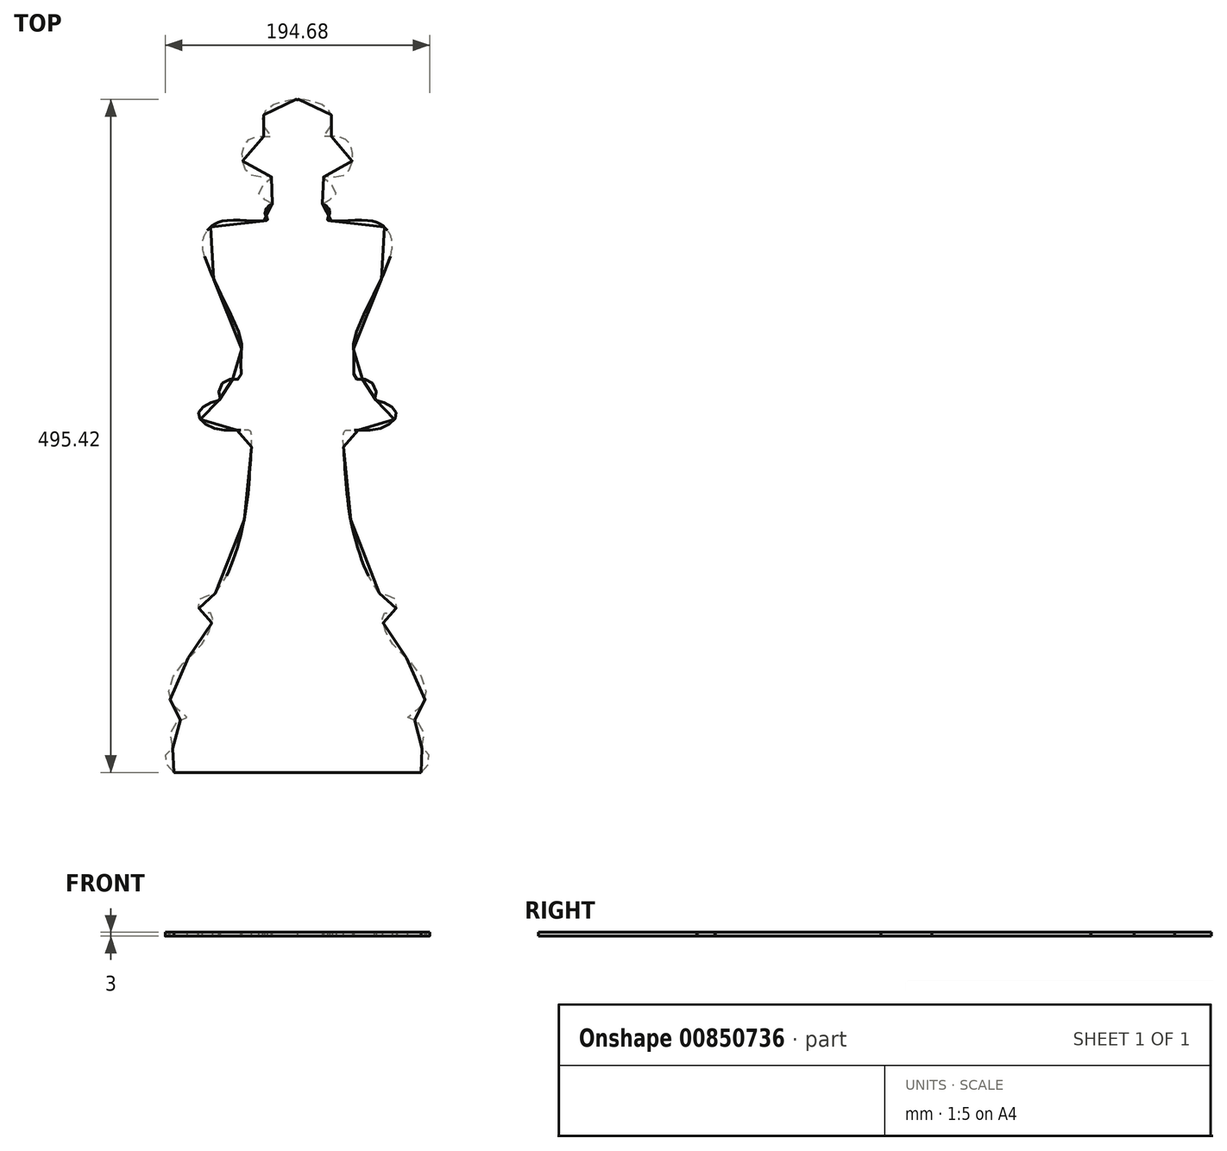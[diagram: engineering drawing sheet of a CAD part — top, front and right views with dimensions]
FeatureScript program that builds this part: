
annotation { "Feature Type Name" : "Feature", "Feature Type Description" : "" }
export const myFeature = defineFeature(function(context is Context, id is Id, definition is map)
    precondition{}
    {
        {
            var Q0;
            Q0=qCreatedBy(makeId("Top.planeOp"),FACE);
            var sketch = newSketch(context, id + "F0", { "sketchPlane" : qUnion([Q0])});
            skLineSegment(sketch, "E0", {"start": v(-250, 250) * mm, "end": v(250, -250) * mm, "construction": true});
            skLineSegment(sketch, "E1", {"start": v(250, 250) * mm, "end": v(-250, -250) * mm, "construction": true});
            skPoint(sketch, "E2", {"position": v(0, 0) * mm});
            skLineSegment(sketch, "E3", {"start": v(0, 250.01) * mm, "end": v(0, -249.99) * mm});
            skLineSegment(sketch, "E4", {"start": v(0, -249.99) * mm, "end": v(-90.99, -249.99) * mm});
            skFitSpline(sketch, "E5", {"points": [v(-90.99, -249.99) * mm, v(-97.06, -242.12) * mm, v(-94.96, -233.93) * mm, v(-90.99, -231.58) * mm, v(-93.32, -226.44) * mm, v(-88.87, -212.86) * mm, v(-80.91, -208.88) * mm, v(-87.93, -204.67) * mm, v(-94.72, -189.45) * mm, v(-84.26, -169.65) * mm, v(-71.55, -157.15) * mm, v(-63.36, -141.47) * mm, v(-63.12, -132.58) * mm, v(-67.34, -133.28) * mm, v(-72.02, -130.24) * mm, v(-72.78, -124.14) * mm, v(-68.58, -119.94) * mm, v(-62.19, -119.47) * mm, v(-41.12, -72.9) * mm, v(-34.34, -16.58) * mm, v(-34.84, 1.46) * mm, v(-38.64, 2.12) * mm, v(-44.77, 2.12) * mm, v(-59.14, 2.94) * mm, v(-71.55, 9.97) * mm, v(-72.25, 16.05) * mm, v(-62.8, 22.6) * mm, v(-56.57, 24.95) * mm, v(-57.84, 27.57) * mm, v(-52.7, 39) * mm, v(-42.76, 39.92) * mm, v(-41.62, 53.72) * mm, v(-42.28, 71.1) * mm, v(-69.2, 133.32) * mm, v(-65.7, 149.7) * mm, v(-51.65, 156.49) * mm, v(-22.16, 156.72) * mm, v(-23.67, 161.1) * mm, v(-21.06, 167.04) * mm, v(-18.42, 168.66) * mm, v(-28.5, 176.52) * mm, v(-19.12, 188.32) * mm, v(-31.3, 188.79) * mm, v(-39.72, 197.45) * mm, v(-39.02, 212.2) * mm, v(-29.42, 218.28) * mm, v(-18.89, 218.28) * mm, v(-23.8, 224.13) * mm, v(-23.1, 237.7) * mm, v(-8.12, 244.73) * mm, v(0, 245.38) * mm], "startDerivative": vector(-423.63, 380.08) * mm, "endDerivative": vector(422.75, -24.47) * mm});
            skFitSpline(sketch, "E6.MirrorCS", {"points": [v(90.99, -249.99) * mm, v(97.06, -242.12) * mm, v(94.96, -233.93) * mm, v(90.99, -231.58) * mm, v(93.32, -226.44) * mm, v(88.87, -212.86) * mm, v(80.91, -208.88) * mm, v(87.93, -204.67) * mm, v(94.72, -189.45) * mm, v(84.26, -169.65) * mm, v(71.55, -157.15) * mm, v(63.36, -141.47) * mm, v(63.12, -132.58) * mm, v(67.34, -133.28) * mm, v(72.02, -130.24) * mm, v(72.78, -124.14) * mm, v(68.58, -119.94) * mm, v(62.19, -119.47) * mm, v(41.12, -72.9) * mm, v(34.34, -16.58) * mm, v(34.84, 1.46) * mm, v(38.64, 2.12) * mm, v(44.77, 2.12) * mm, v(59.14, 2.94) * mm, v(71.55, 9.97) * mm, v(72.25, 16.05) * mm, v(62.8, 22.6) * mm, v(56.57, 24.95) * mm, v(57.84, 27.57) * mm, v(52.7, 39) * mm, v(42.76, 39.92) * mm, v(41.62, 53.72) * mm, v(42.28, 71.1) * mm, v(69.2, 133.32) * mm, v(65.7, 149.7) * mm, v(51.65, 156.49) * mm, v(22.16, 156.72) * mm, v(23.67, 161.1) * mm, v(21.06, 167.04) * mm, v(18.42, 168.66) * mm, v(28.5, 176.52) * mm, v(19.12, 188.32) * mm, v(31.3, 188.79) * mm, v(39.72, 197.45) * mm, v(39.02, 212.2) * mm, v(29.42, 218.28) * mm, v(18.89, 218.28) * mm, v(23.8, 224.13) * mm, v(23.1, 237.7) * mm, v(8.12, 244.73) * mm, v(0, 245.38) * mm], "startDerivative": vector(423.63, 380.08) * mm, "endDerivative": vector(-422.75, -24.47) * mm});
            skLineSegment(sketch, "E7.MirrorCS", {"start": v(0, -249.99) * mm, "end": v(90.99, -249.99) * mm});
            skLineSegment(sketch, "E8.bottom", {"start": v(-1, 249.99) * mm, "end": v(1, 249.99) * mm});
            skLineSegment(sketch, "E8.top", {"start": v(-1, -249.99) * mm, "end": v(1, -249.99) * mm});
            skLineSegment(sketch, "E8.left", {"start": v(-1, 249.99) * mm, "end": v(-1, -249.99) * mm});
            skLineSegment(sketch, "E8.right", {"start": v(1, 249.99) * mm, "end": v(1, -249.99) * mm});
            skLineSegment(sketch, "E9", {"start": v(-1, 0) * mm, "end": v(1, 0) * mm});
            skSolve(sketch);
        }
        {
            var Q0;
            {var subQ0=sQuery(id+"F0.wireOp",EDGE,"E7.MirrorCS");Q0=makeQuery(id+"F0.imprint","IMPRINT",FACE,{"disambiguationData":[TD([[makeQuery(id+"F0.imprint","IMPRINT",EDGE,{"derivedFrom":subQ0}),1.0]])]});}
            var Q1;
            {var subQ0=sQuery(id+"F0.wireOp",EDGE,"E4");Q1=makeQuery(id+"F0.imprint","IMPRINT",FACE,{"disambiguationData":[TD([[makeQuery(id+"F0.imprint","IMPRINT",EDGE,{"derivedFrom":subQ0}),-1.0]])]});}
            var Q2;
            {var subQ3=sQuery(id+"F0.wireOp",EDGE,"E9");var subQ5=sQuery(id+"F0.wireOp",EDGE,"E8.right");var subQ7=makeQuery(id+"F0.imprint","INTERSECT",VERTEX,{"derivedFrom":[subQ5,subQ3]});Q2=makeQuery(id+"F0.imprint","IMPRINT",FACE,{"disambiguationData":[TD([[makeQuery(id+"F0.imprint","IMPRINT",EDGE,{"disambiguationData":[TD([[subQ7,1.0]])],"derivedFrom":subQ5}),-1.0]])]});}
            var Q3;
            {var subQ3=sQuery(id+"F0.wireOp",EDGE,"E9");var subQ5=sQuery(id+"F0.wireOp",EDGE,"E8.left");var subQ7=makeQuery(id+"F0.imprint","INTERSECT",VERTEX,{"derivedFrom":[subQ5,subQ3]});Q3=makeQuery(id+"F0.imprint","IMPRINT",FACE,{"disambiguationData":[TD([[makeQuery(id+"F0.imprint","IMPRINT",EDGE,{"disambiguationData":[TD([[subQ7,1.0]])],"derivedFrom":subQ5}),1.0]])]});}
            extrude(context, id + "F1", {"entities" : qUnion([Q0, Q1, Q2, Q3]), "depth" : 3 * mm, "offsetDistance" : 25 * mm});
        }
    });
